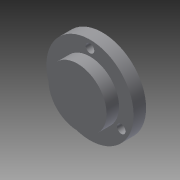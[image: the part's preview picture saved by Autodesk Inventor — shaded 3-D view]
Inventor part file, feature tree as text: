
AUTODESK INVENTOR PART (.ipt)
format: ipt  version: 2015 (Build 190159000, 159)  size: 97,280 bytes
history: native  units: in
note: dims shown in document units (in); Inventor stores cm internally (conversion verified against a paired STEP export)
features: sketch x3, extrude x2, hole x1
ambient origin geometry x8: Origin, YZ Plane, XZ Plane, XY Plane, X Axis, Y Axis, Z Axis, Center Point
bodies: Solid1 (feature_tree)
feature tree (6):
  extrude  "Extrusion1"  Depth=0.25in TaperAngle=0.0deg
  extrude  "Extrusion2"  Depth=0.25in TaperAngle=0.0deg
  hole  "Hole1"  [1 undecoded]
  sketch  "Sketch1"  dims[d0=1.75in d1=0.25in d2=0.0in]
  sketch  "Sketch2"  dims[d3=1.165in d4=0.25in d5=0.0in]
  sketch  "Sketch4"  dims[d12=1.1811in d14=360.0deg d16=0.172in d17=0.75in d18=0.375in d19=0.25in d20=0.5635in d21=1.0in d22=0.8108in]
note: 1 required parameter value undecoded (feature->parameter linkage not recoverable at this tier; creation-order binding heuristic only, values carry confidence <= 0.55)
